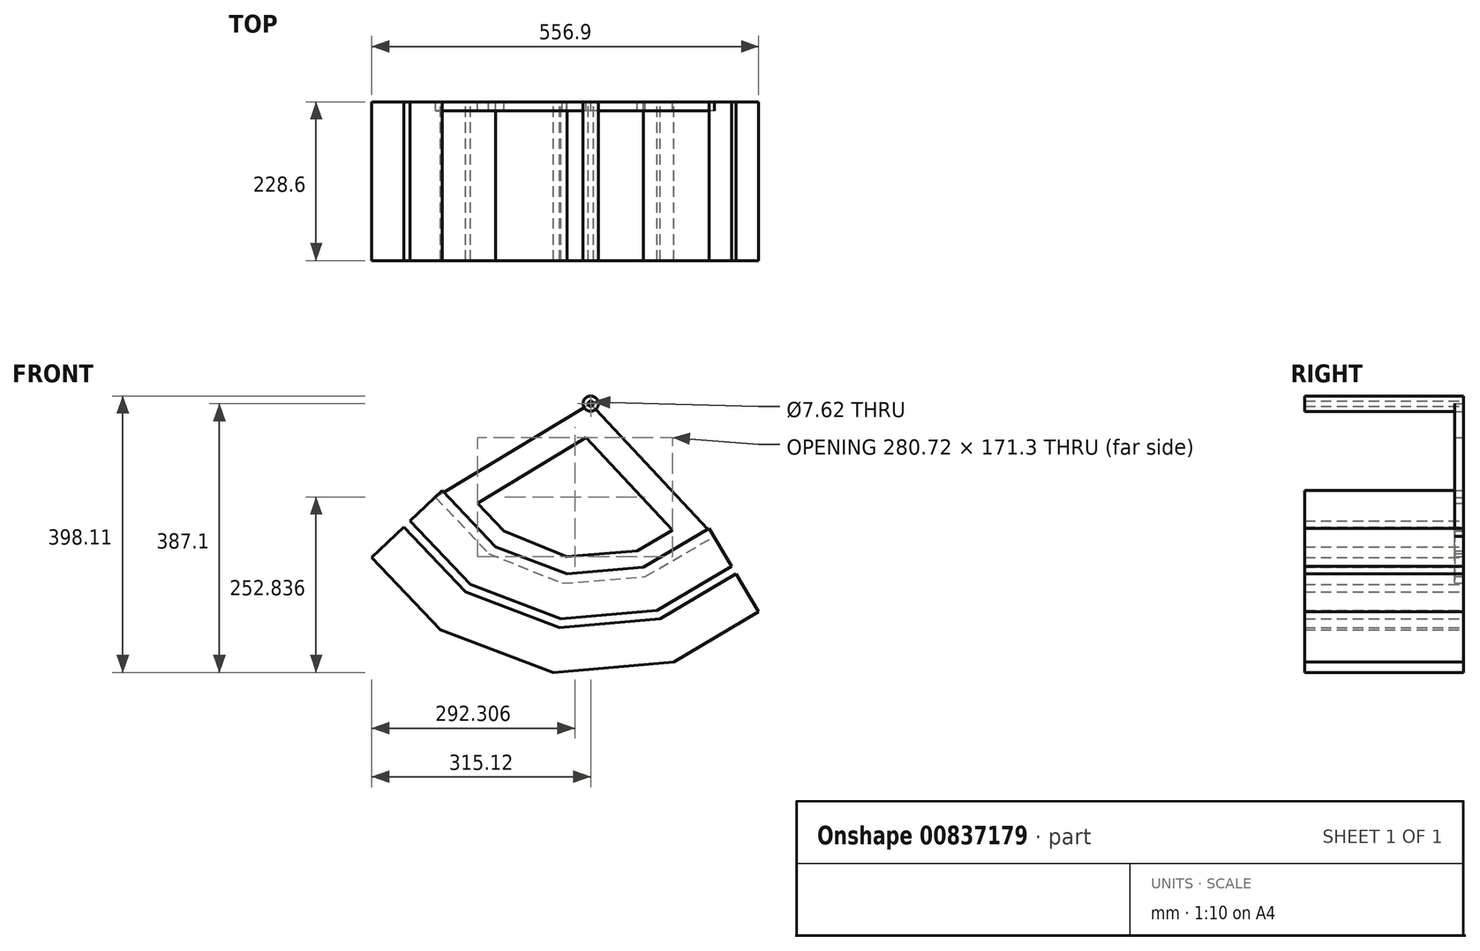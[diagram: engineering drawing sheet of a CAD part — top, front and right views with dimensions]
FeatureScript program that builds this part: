
annotation { "Feature Type Name" : "Feature", "Feature Type Description" : "" }
export const myFeature = defineFeature(function(context is Context, id is Id, definition is map)
    precondition{}
    {
        {
            var Q0;
            Q0=qCreatedBy(makeId("Front.planeOp"),FACE);
            var sketch = newSketch(context, id + "F0", { "sketchPlane" : qUnion([Q0])});
            skCircle(sketch, "E0", {"center": v(0, 0) * mm, "radius": 3.81 * mm});
            skCircle(sketch, "E1", {"center": v(0, 0) * mm, "radius": 11.01 * mm});
            skCircle(sketch, "E2.cCircle", {"center": v(0, 0) * mm, "radius": 241.3 * mm, "construction": true});
            skLineSegment(sketch, "E2.0", {"start": v(170.5, -179.42) * mm, "end": v(75.76, -235.63) * mm});
            skLineSegment(sketch, "E2.1", {"start": v(75.76, -235.63) * mm, "end": v(-33.98, -245.16) * mm});
            skLineSegment(sketch, "E2.2", {"start": v(-33.98, -245.16) * mm, "end": v(-136.98, -206.14) * mm});
            skLineSegment(sketch, "E2.3", {"start": v(-136.98, -206.14) * mm, "end": v(-213.85, -125.25) * mm});
            skPoint(sketch, "E2.0.midPoint", {"position": v(123.13, -207.52) * mm});
            skLineSegment(sketch, "E3.0", {"start": v(-144.2, -217) * mm, "end": v(-223.06, -134) * mm});
            skLineSegment(sketch, "E3.1", {"start": v(-35.76, -258.07) * mm, "end": v(-144.2, -217) * mm});
            skLineSegment(sketch, "E3.2", {"start": v(79.75, -248.03) * mm, "end": v(-35.76, -258.07) * mm});
            skLineSegment(sketch, "E3.3", {"start": v(176.97, -190.34) * mm, "end": v(79.75, -248.03) * mm});
            skLineSegment(sketch, "E4.0", {"start": v(-173.03, -260.4) * mm, "end": v(-259.89, -168.99) * mm});
            skLineSegment(sketch, "E4.1", {"start": v(-42.92, -309.68) * mm, "end": v(-173.03, -260.4) * mm});
            skLineSegment(sketch, "E4.2", {"start": v(95.7, -297.63) * mm, "end": v(-42.92, -309.68) * mm});
            skLineSegment(sketch, "E4.3", {"start": v(202.9, -234.03) * mm, "end": v(95.7, -297.63) * mm});
            skLineSegment(sketch, "E5", {"start": v(-259.89, -168.99) * mm, "end": v(-213.85, -125.25) * mm});
            skLineSegment(sketch, "E6", {"start": v(170.5, -179.42) * mm, "end": v(202.9, -234.03) * mm});
            skSolve(sketch);
        }
        {
            var Q0;
            Q0=qCreatedBy(makeId("Front.planeOp"),FACE);
            var sketch = newSketch(context, id + "F1", { "sketchPlane" : qUnion([Q0])});
            skLineSegment(sketch, "E7.0", {"start": v(-180.24, -271.24) * mm, "end": v(-269.1, -177.73) * mm});
            skLineSegment(sketch, "E7.1", {"start": v(-44.7, -322.58) * mm, "end": v(-180.24, -271.24) * mm});
            skLineSegment(sketch, "E7.2", {"start": v(99.69, -310.03) * mm, "end": v(-44.7, -322.58) * mm});
            skLineSegment(sketch, "E7.3", {"start": v(209.37, -244.95) * mm, "end": v(99.69, -310.03) * mm});
            skLineSegment(sketch, "E8.0", {"start": v(-209.08, -314.64) * mm, "end": v(-305.92, -212.73) * mm});
            skLineSegment(sketch, "E8.1", {"start": v(-51.86, -374.2) * mm, "end": v(-209.08, -314.64) * mm});
            skLineSegment(sketch, "E8.2", {"start": v(115.63, -359.64) * mm, "end": v(-51.86, -374.2) * mm});
            skLineSegment(sketch, "E8.3", {"start": v(235.3, -288.64) * mm, "end": v(115.63, -359.64) * mm});
            skLineSegment(sketch, "E9", {"start": v(-305.92, -212.73) * mm, "end": v(-269.1, -177.73) * mm});
            skLineSegment(sketch, "E10", {"start": v(209.37, -244.95) * mm, "end": v(235.3, -288.64) * mm});
            skLineSegment(sketch, "E11", {"start": v(-44.7, -322.58) * mm, "end": v(-51.86, -374.2) * mm});
            skLineSegment(sketch, "E12", {"start": v(-180.24, -271.24) * mm, "end": v(-209.08, -314.64) * mm});
            skLineSegment(sketch, "E13", {"start": v(99.69, -310.03) * mm, "end": v(115.63, -359.64) * mm});
            skLineSegment(sketch, "E14.0", {"start": v(-216.29, -325.49) * mm, "end": v(-315.12, -221.48) * mm});
            skLineSegment(sketch, "E14.1", {"start": v(-53.65, -387.1) * mm, "end": v(-216.29, -325.49) * mm});
            skLineSegment(sketch, "E14.2", {"start": v(119.62, -372.04) * mm, "end": v(-53.65, -387.1) * mm});
            skLineSegment(sketch, "E14.3", {"start": v(241.78, -299.56) * mm, "end": v(119.62, -372.04) * mm});
            skLineSegment(sketch, "E15", {"start": v(-315.12, -221.48) * mm, "end": v(-305.92, -212.73) * mm});
            skLineSegment(sketch, "E16", {"start": v(241.78, -299.56) * mm, "end": v(235.3, -288.64) * mm});
            skSolve(sketch);
        }
        {
            var Q0;
            Q0=makeQuery(id+"F0.imprint","IMPRINT",FACE,{"disambiguationData":[TD([[makeQuery(id+"F0.imprint","IMPRINT",EDGE,{"derivedFrom":sQuery(id+"F0.wireOp",EDGE,"E0")}),-1.0]])]});
            var Q1;
            {var subQ1=sQuery(id+"F0.wireOp",EDGE,"E3.0");Q1=makeQuery(id+"F0.imprint","IMPRINT",FACE,{"disambiguationData":[TD([[makeQuery(id+"F0.imprint","IMPRINT",EDGE,{"derivedFrom":subQ1}),1.0]])]});}
            var Q2;
            {var subQ2=sQuery(id+"F0.wireOp",EDGE,"E2.0");Q2=makeQuery(id+"F0.imprint","IMPRINT",FACE,{"disambiguationData":[TD([[makeQuery(id+"F0.imprint","IMPRINT",EDGE,{"derivedFrom":subQ2}),1.0]])]});}
            extrude(context, id + "F2", {"entities" : qUnion([Q0, Q1, Q2]), "depth" : 228.6 * mm, "offsetDistance" : 25.4 * mm});
        }
        {
            var Q0;
            Q0 = qSketchRegion(id + "F1", true);
            extrude(context, id + "F3", {"entities" : qUnion([Q0]), "depth" : 228.6 * mm, "offsetDistance" : 25.4 * mm});
        }
        {
            var Q0;
            Q0=qCreatedBy(makeId("Front.planeOp"),FACE);
            var sketch = newSketch(context, id + "F4", { "sketchPlane" : qUnion([Q0])});
            skLineSegment(sketch, "E17", {"start": v(0, 0) * mm, "end": v(-223.3, -134.86) * mm});
            skLineSegment(sketch, "E18", {"start": v(-223.3, -134.86) * mm, "end": v(-146.88, -215.85) * mm});
            skLineSegment(sketch, "E19", {"start": v(-146.88, -215.85) * mm, "end": v(-40.88, -258.61) * mm});
            skLineSegment(sketch, "E20", {"start": v(-40.88, -258.61) * mm, "end": v(78.5, -248.99) * mm});
            skLineSegment(sketch, "E21", {"start": v(78.5, -248.99) * mm, "end": v(177.93, -191.14) * mm});
            skLineSegment(sketch, "E22", {"start": v(177.93, -191.14) * mm, "end": v(0, 0) * mm});
            skLineSegment(sketch, "E23.0", {"start": v(117.55, -182.19) * mm, "end": v(-6.8, -48.62) * mm});
            skLineSegment(sketch, "E23.1", {"start": v(-163.17, -143.06) * mm, "end": v(-124.89, -183.64) * mm});
            skLineSegment(sketch, "E23.2", {"start": v(-124.89, -183.64) * mm, "end": v(-34.97, -219.91) * mm});
            skLineSegment(sketch, "E23.3", {"start": v(-6.8, -48.62) * mm, "end": v(-163.17, -143.06) * mm});
            skLineSegment(sketch, "E23.4", {"start": v(-34.97, -219.91) * mm, "end": v(66.81, -211.7) * mm});
            skLineSegment(sketch, "E23.5", {"start": v(66.81, -211.7) * mm, "end": v(117.55, -182.19) * mm});
            skSolve(sketch);
        }
        {
            var Q0;
            Q0 = qSketchRegion(id + "F4", true);
            extrude(context, id + "F5", {"entities" : qUnion([Q0]), "depth" : 12.7 * mm, "offsetDistance" : 25.4 * mm});
        }
    });
